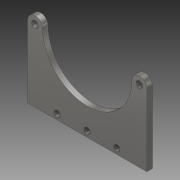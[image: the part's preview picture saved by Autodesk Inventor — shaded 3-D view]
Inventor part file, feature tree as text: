
AUTODESK INVENTOR PART (.ipt)
format: ipt  version: 2019 (Build 230136000, 136)  size: 115,712 bytes
history: native  units: mm
features: sketch x2, extrude x1, hole x1, projected_geometry x1
ambient origin geometry x8: Origin, YZ Plane, XZ Plane, XY Plane, X Axis, Y Axis, Z Axis, Center Point
bodies: Solid1 (feature_tree)
feature tree (5):
  extrude  "Extrusion1"  Depth=108.0mm
  hole  "Hole1"  [1 undecoded]
  sketch  "Sketch1"  dims[d0=108.0mm d2=6.0mm]
  sketch  "Sketch2"  dims[d3=6.0mm d6=94.5mm d9=65.0mm d10=5.0mm d11=0.0mm d12=5.0mm d13=54.0mm d14=5.5mm d15=10.0mm d16=8.0mm d17=2.0mm d18=90.0deg d19=14.2mm d20=20.594885mm]
  projected_geometry  "Projected Loop1"
note: 1 required parameter value undecoded (feature->parameter linkage not recoverable at this tier; creation-order binding heuristic only, values carry confidence <= 0.55)
